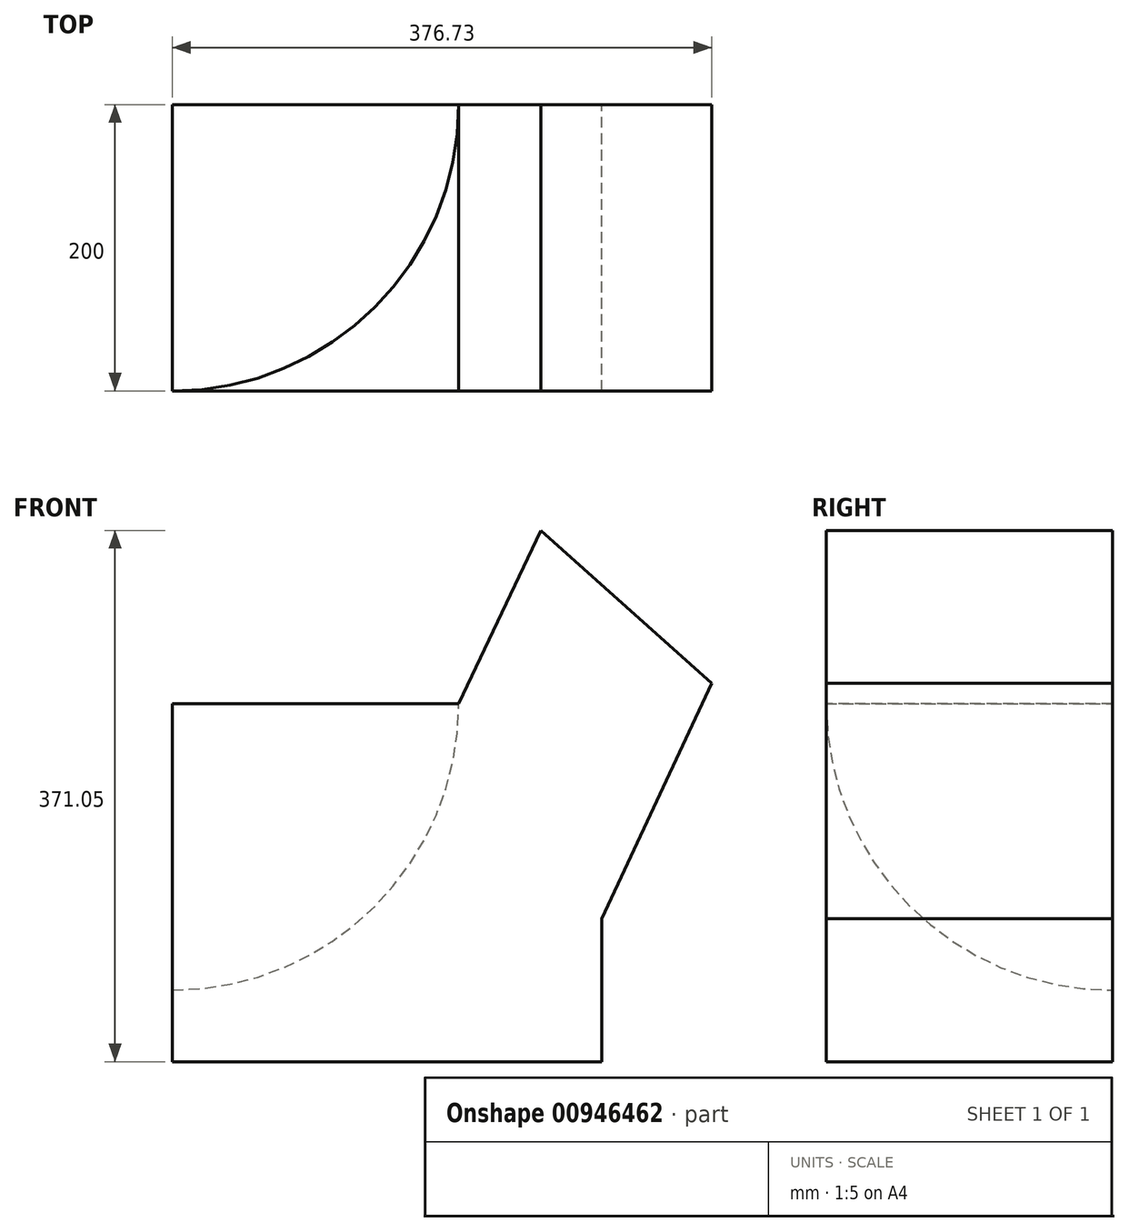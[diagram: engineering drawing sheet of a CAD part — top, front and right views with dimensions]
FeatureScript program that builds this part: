
annotation { "Feature Type Name" : "Feature", "Feature Type Description" : "" }
export const myFeature = defineFeature(function(context is Context, id is Id, definition is map)
    precondition{}
    {
        {
            var Q0;
            Q0=qCreatedBy(makeId("Front.planeOp"),FACE);
            var sketch = newSketch(context, id + "F0", { "sketchPlane" : qUnion([Q0])});
            skLineSegment(sketch, "E0.bottom", {"start": v(0, 0) * mm, "end": v(0, 0) * mm});
            skLineSegment(sketch, "E0.top", {"start": v(0, 0) * mm, "end": v(0, 0) * mm});
            skLineSegment(sketch, "E0.left", {"start": v(0, 0) * mm, "end": v(0, 0) * mm});
            skLineSegment(sketch, "E0.right", {"start": v(0, 0) * mm, "end": v(0, 0) * mm});
            skLineSegment(sketch, "E1.bottom", {"start": v(300, -250) * mm, "end": v(0, -250) * mm});
            skLineSegment(sketch, "E1.top", {"start": v(300, 0) * mm, "end": v(0, 0) * mm});
            skLineSegment(sketch, "E1.left", {"start": v(300, -250) * mm, "end": v(300, 0) * mm});
            skLineSegment(sketch, "E1.right", {"start": v(0, -250) * mm, "end": v(0, 0) * mm});
            skSolve(sketch);
        }
        {
            var Q0;
            Q0 = qSketchRegion(id + "F0", true);
            extrude(context, id + "F1", {"entities" : qUnion([Q0]), "depth" : 200 * mm, "offsetDistance" : 25 * mm});
        }
        {
            var Q0;
            Q0=qCreatedBy(makeId("Front.planeOp"),FACE);
            var sketch = newSketch(context, id + "F2", { "sketchPlane" : qUnion([Q0])});
            skLineSegment(sketch, "E2", {"start": v(200, 0) * mm, "end": v(300, -150) * mm});
            skLineSegment(sketch, "E3", {"start": v(200, 0) * mm, "end": v(257.49, 121.05) * mm});
            skLineSegment(sketch, "E4", {"start": v(257.49, 121.05) * mm, "end": v(376.73, 14.41) * mm});
            skLineSegment(sketch, "E5", {"start": v(376.73, 14.41) * mm, "end": v(300, -150) * mm});
            skSolve(sketch);
        }
        {
            var Q0;
            Q0 = qSketchRegion(id + "F2", true);
            extrude(context, id + "F3", {"entities" : qUnion([Q0]), "operationType" : NewBodyOperationType.ADD, "depth" : 200 * mm, "offsetDistance" : 25 * mm});
        }
        {
            var Q0;
            Q0=qCreatedBy(makeId("Top.planeOp"),FACE);
            var sketch = newSketch(context, id + "F4", { "sketchPlane" : qUnion([Q0])});
            skArc(sketch, "E6", {"start": v(0, 200) * mm, "mid": v(-200, 0) * mm, "end": v(0, -200) * mm});
            skLineSegment(sketch, "E7", {"start": v(0, 308) * mm, "end": v(0, -302.13) * mm});
            skSolve(sketch);
        }
        {
            var Q0;
            {var subQ0=sQuery(id+"F4.wireOp",EDGE,"E6");Q0=makeQuery(id+"F4.imprint","IMPRINT",FACE,{"disambiguationData":[TD([[makeQuery(id+"F4.imprint","IMPRINT",EDGE,{"derivedFrom":subQ0}),1.0]])]});}
            var Q1;
            Q1=sQuery(id+"F4.wireOp",EDGE,"E7");
            revolve(context, id + "F5", {"operationType" : NewBodyOperationType.ADD, "surfaceOperationType" : NewSurfaceOperationType.NEW, "entities" : qUnion([Q0]), "axis" : qUnion([Q1]), "revolveType" : RevolveType.FULL});
        }
    });
